# Revit family: 63_UN_LEDPanel_CoreLine panel G5 W30L120 SM_Signify
name_source: partatom
category: Lighting Fixtures
units: mm (PartAtom-declared; Revit-internal decimal feet)

## family parameters
Always vertical = Yes
Cut with Voids When Loaded = No
Light Source = Yes
OmniClass Number = 23.80.70.11.14.11
OmniClass Title = Downlights
Part Type = Normal
Room Calculation Point = Yes
Round Connector Dimension = Use Diameter
Shared = No
Work Plane-Based = No

## types (4) — shared parameters
Apparent Load = 34 VA
Assembly Code = 63.0
Calc_L1_Symbol = 12 mm  [stored 0.0393701 ft]
Calc_L2_Symbol = 3 mm  [stored 0.00984252 ft]
Color Filter = 16777215
Dimming Lamp Color Temperature Shift = <None>
Emit Shape Visible in Rendering = No
Emit from Rectangle Length = 1155 mm  [stored 3.78937 ft]
Emit from Rectangle Width = 255 mm  [stored 0.836614 ft]
Housing_Material = Laminate, White
IK Value = IK02
IP Value = IP20
IfcExportAs = IfcLightFixtureType
IfcExportType = USERDEFINED
Lamp = LED
Luminous Flux (lm) = 3600 lm
Manufacturer = Signify
Model = Coreline Panel
Photometric Web File = ES-M-PS-12S-827-PSD-MB-ALL-ALL.ies
Tilt Angle = 90.00°
Type Comments = G5 W30L120
URL = https://www.ivlibrary.com
Voltage = 230 V
Wattage Comments = 34W

## type names (no varying parameters)
- W30L120 PSD OC
- W30L120 PSU NOC
- W30L120 PSU OC
- 30120_WIA

note: [stored X ft] marks values corroborated as IEEE doubles in the binary element streams (Revit-internal decimal feet)

## geometry (parser evidence)
native form markers: Sweep x1
no freeform markers — native parametric forms only
